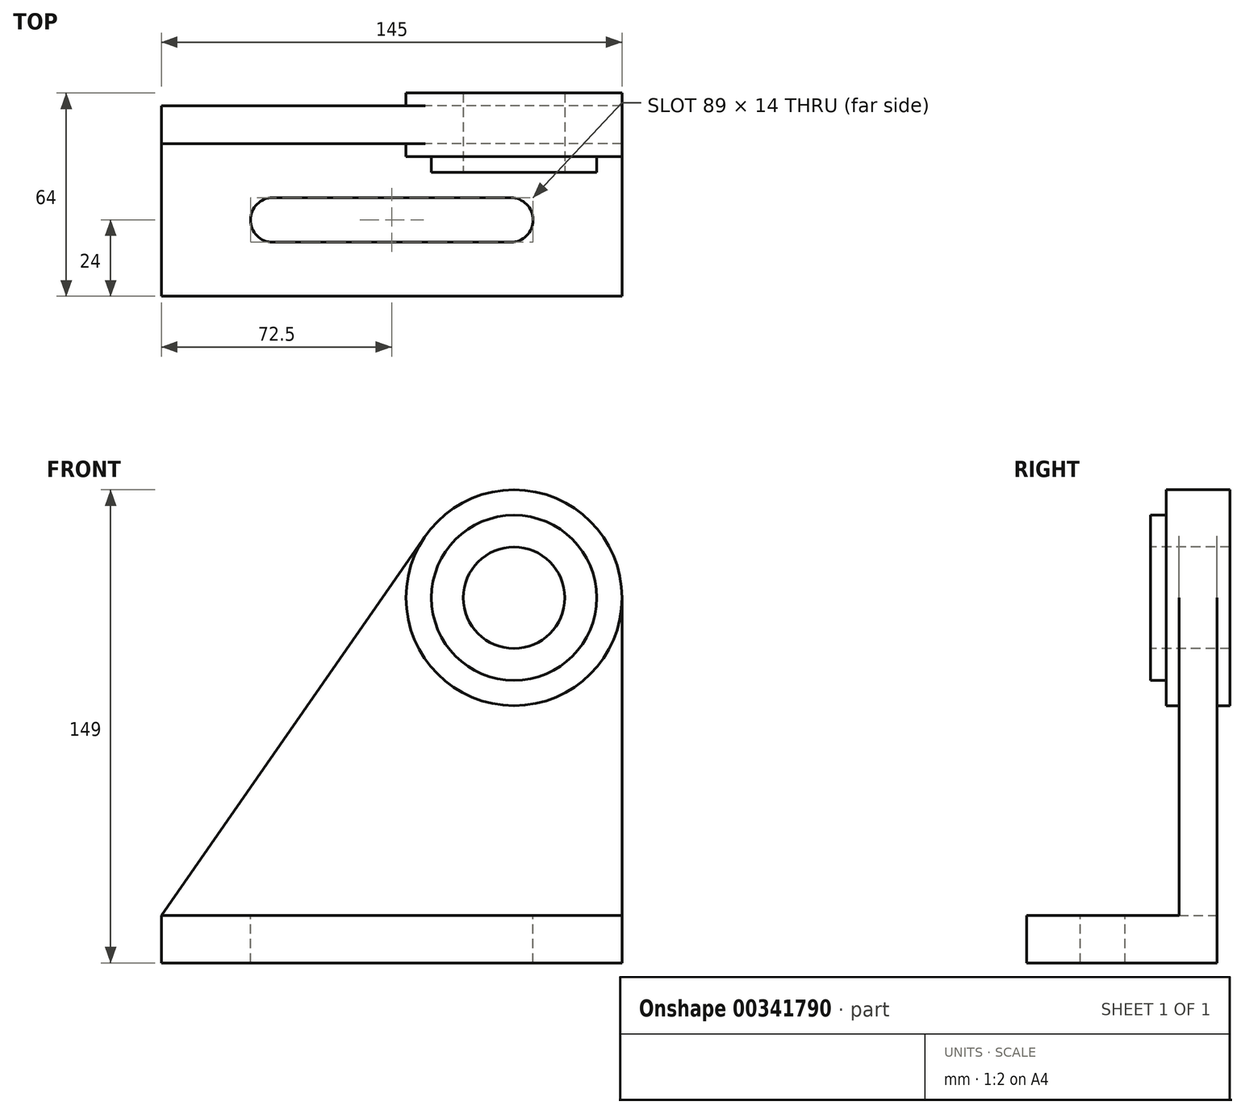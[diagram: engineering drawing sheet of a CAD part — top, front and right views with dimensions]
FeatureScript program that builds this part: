
annotation { "Feature Type Name" : "Feature", "Feature Type Description" : "" }
export const myFeature = defineFeature(function(context is Context, id is Id, definition is map)
    precondition{}
    {
        {
            var Q0;
            Q0=qCreatedBy(makeId("Top.planeOp"),FACE);
            var sketch = newSketch(context, id + "F0", { "sketchPlane" : qUnion([Q0])});
            skLineSegment(sketch, "E0", {"start": v(0, 0) * mm, "end": v(-72.5, 0) * mm, "construction": true});
            skLineSegment(sketch, "E1", {"start": v(-72.5, 0) * mm, "end": v(-72.5, -24) * mm});
            skLineSegment(sketch, "E2", {"start": v(-72.5, -24) * mm, "end": v(-37.5, -24) * mm});
            skLineSegment(sketch, "E3", {"start": v(-37.5, -24) * mm, "end": v(37.5, -24) * mm});
            skLineSegment(sketch, "E4", {"start": v(37.5, -24) * mm, "end": v(72.5, -24) * mm});
            skLineSegment(sketch, "E5", {"start": v(72.5, -24) * mm, "end": v(72.5, 0) * mm});
            skLineSegment(sketch, "E6", {"start": v(72.5, 0) * mm, "end": v(72.5, 24) * mm});
            skLineSegment(sketch, "E7", {"start": v(72.5, 24) * mm, "end": v(-72.5, 24) * mm});
            skLineSegment(sketch, "E8", {"start": v(-72.5, 24) * mm, "end": v(-72.5, 0) * mm});
            skLineSegment(sketch, "E9", {"start": v(-37.5, -24) * mm, "end": v(-37.5, 0) * mm, "construction": true});
            skCircle(sketch, "E10.MirrorC", {"center": v(37.5, 0) * mm, "radius": 7 * mm, "construction": true});
            skLineSegment(sketch, "E11", {"start": v(-37.5, -7) * mm, "end": v(37.5, -7) * mm});
            skArc(sketch, "E12", {"start": v(-37.5, 7) * mm, "mid": v(-44.5, 0) * mm, "end": v(-37.5, -7) * mm});
            skArc(sketch, "E13.MirrorCS", {"start": v(37.5, 7) * mm, "mid": v(44.5, 0) * mm, "end": v(37.5, -7) * mm});
            skLineSegment(sketch, "E14.MirrorCS", {"start": v(-37.5, 7) * mm, "end": v(37.5, 7) * mm});
            skLineSegment(sketch, "E15", {"start": v(-72.5, 24) * mm, "end": v(-72.5, 36) * mm});
            skLineSegment(sketch, "E16", {"start": v(-72.5, 36) * mm, "end": v(72.5, 36) * mm});
            skLineSegment(sketch, "E17", {"start": v(72.5, 36) * mm, "end": v(72.5, 24) * mm});
            skSolve(sketch);
        }
        {
            var Q0;
            Q0=makeQuery(id+"F0.imprint","IMPRINT",FACE,{"disambiguationData":[TD([[makeQuery(id+"F0.imprint","IMPRINT",EDGE,{"derivedFrom":sQuery(id+"F0.wireOp",EDGE,"E7")}),-1.0]])]});
            var Q1;
            Q1=makeQuery(id+"F0.imprint","IMPRINT",FACE,{"disambiguationData":[TD([[makeQuery(id+"F0.imprint","IMPRINT",EDGE,{"derivedFrom":sQuery(id+"F0.wireOp",EDGE,"E1")}),1.0]])]});
            extrude(context, id + "F1", {"entities" : qUnion([Q0, Q1]), "oppositeDirection" : true, "depth" : 15 * mm});
        }
        {
            var Q0;
            Q0=makeQuery(id+"F1.opExtrude","SWEPT_FACE",FACE,{"disambiguationData":[OSD([sQuery(id+"F0.wireOp",EDGE,"E16")])]});
            cPlane(context, id + "F2", {"entities" : qUnion([Q0]), "cplaneType" : CPlaneType.OFFSET, "offset" : 0 * mm, "width" : 150 * mm, "height" : 150 * mm});
        }
        {
            var Q0;
            Q0=qCreatedBy(id+"F2.planeOp",FACE);
            var sketch = newSketch(context, id + "F3", { "sketchPlane" : qUnion([Q0])});
            skCircle(sketch, "E18", {"center": v(-38.5, 100) * mm, "radius": 34 * mm});
            skLineSegment(sketch, "E19", {"start": v(-72.5, 0) * mm, "end": v(-72.5, 100) * mm});
            skLineSegment(sketch, "E20", {"start": v(72.5, 0) * mm, "end": v(-10.6, 119.42) * mm});
            skCircle(sketch, "E21", {"center": v(-38.5, 100) * mm, "radius": 26 * mm});
            skCircle(sketch, "E22", {"center": v(-38.5, 100) * mm, "radius": 16 * mm});
            skLineSegment(sketch, "E23", {"start": v(72.5, 0) * mm, "end": v(-72.5, 0) * mm});
            skSolve(sketch);
        }
        {
            var Q0;
            {var subQ0=sQuery(id+"F3.wireOp",EDGE,"E19");Q0=makeQuery(id+"F3.imprint","IMPRINT",FACE,{"disambiguationData":[TD([[makeQuery(id+"F3.imprint","IMPRINT",EDGE,{"derivedFrom":subQ0}),-1.0]])]});}
            extrude(context, id + "F4", {"entities" : qUnion([Q0]), "operationType" : NewBodyOperationType.ADD, "oppositeDirection" : true, "depth" : 12 * mm});
        }
        {
            var Q0;
            Q0=makeQuery(id+"F4.boolean.opBoolean","MERGE",FACE,{"derivedFrom":[makeQuery(id+"F1.opExtrude","SWEPT_FACE",FACE,{"disambiguationData":[OSD([sQuery(id+"F0.wireOp",EDGE,"E16")])]}),makeQuery(id+"F4.opExtrude","CAP_FACE",FACE,{"disambiguationData":[OSD([sQuery(id+"F3.wireOp",EDGE,"E18"),sQuery(id+"F3.wireOp",EDGE,"E19"),sQuery(id+"F3.wireOp",EDGE,"E20"),sQuery(id+"F3.wireOp",EDGE,"E23")])],"isStart":true})]});
            cPlane(context, id + "F5", {"entities" : qUnion([Q0]), "cplaneType" : CPlaneType.OFFSET, "offset" : (12 / 2) * mm, "oppositeDirection" : true, "width" : 150 * mm, "height" : 150 * mm});
        }
        {
            var Q0;
            Q0=qCreatedBy(id+"F5.planeOp",FACE);
            var sketch = newSketch(context, id + "F6", { "sketchPlane" : qUnion([Q0])});
            skCircle(sketch, "E24", {"center": v(-38.5, 100) * mm, "radius": 34 * mm});
            skLineSegment(sketch, "E25", {"start": v(72.5, 0) * mm, "end": v(-10.65, 119.5) * mm, "construction": true});
            skLineSegment(sketch, "E26", {"start": v(-72.5, 0) * mm, "end": v(-72.5, 100) * mm});
            skCircle(sketch, "E27", {"center": v(-38.5, 100) * mm, "radius": 26 * mm});
            skCircle(sketch, "E28", {"center": v(-38.5, 100) * mm, "radius": 16 * mm});
            skSolve(sketch);
        }
        {
            var Q0;
            Q0=makeQuery(id+"F6.imprint","IMPRINT",FACE,{"disambiguationData":[TD([[makeQuery(id+"F6.imprint","IMPRINT",EDGE,{"derivedFrom":sQuery(id+"F6.wireOp",EDGE,"E24")}),1.0]])]});
            var Q1;
            Q1=makeQuery(id+"F6.imprint","IMPRINT",FACE,{"disambiguationData":[TD([[makeQuery(id+"F6.imprint","IMPRINT",EDGE,{"derivedFrom":sQuery(id+"F6.wireOp",EDGE,"E27")}),1.0]])]});
            extrude(context, id + "F7", {"entities" : qUnion([Q0, Q1]), "operationType" : NewBodyOperationType.ADD, "depth" : 10 * mm});
        }
        {
            var Q0;
            Q0=makeQuery(id+"F6.imprint","IMPRINT",FACE,{"disambiguationData":[TD([[makeQuery(id+"F6.imprint","IMPRINT",EDGE,{"derivedFrom":sQuery(id+"F6.wireOp",EDGE,"E24")}),1.0]])]});
            extrude(context, id + "F8", {"entities" : qUnion([Q0]), "operationType" : NewBodyOperationType.ADD, "oppositeDirection" : true, "depth" : 10 * mm});
        }
        {
            var Q0;
            Q0=makeQuery(id+"F6.imprint","IMPRINT",FACE,{"disambiguationData":[TD([[makeQuery(id+"F6.imprint","IMPRINT",EDGE,{"derivedFrom":sQuery(id+"F6.wireOp",EDGE,"E27")}),1.0]])]});
            extrude(context, id + "F9", {"entities" : qUnion([Q0]), "operationType" : NewBodyOperationType.ADD, "oppositeDirection" : true, "depth" : 15 * mm});
        }
    });
